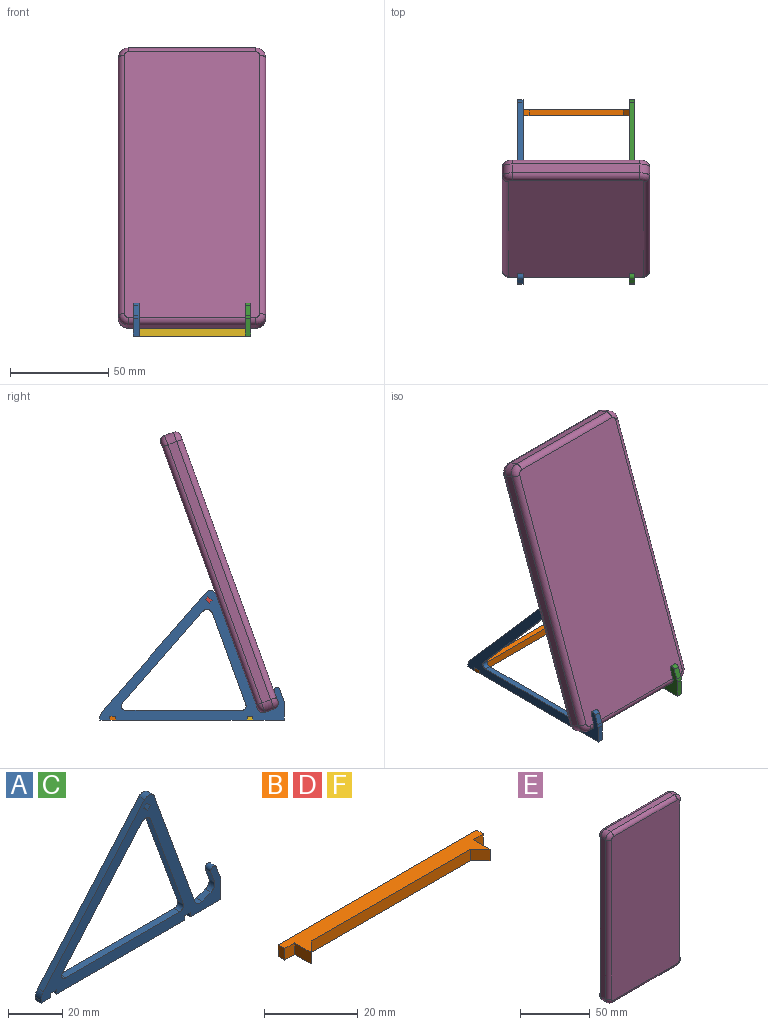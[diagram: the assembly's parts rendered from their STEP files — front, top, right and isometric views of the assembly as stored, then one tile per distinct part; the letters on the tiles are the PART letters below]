
ASSEMBLY  parts=6 mates=15
PART A: 34 faces, bbox 93.9x3x66 mm
  f0: plane 67x3mm, normal (0,0,-1), area 201mm2, adj f2,f3,f24,f28
  f1: plane 15.88x3mm, normal (0,0,-1), area 47.6mm2, adj f2,f3,f14,f25
  f2: plane 93.88x65.98mm, normal (0,-1,0), area 1195.2mm2, adj f0,f1,f4,f5,f6,f7,f8,f9
  f3: plane 93.88x65.98mm, normal (0,1,0), area 1195.2mm2, adj f0,f1,f4,f5,f6,f7,f8,f9
  f4: plane 5x3mm, normal (0,0,-1), area 15mm2, adj f2,f3,f13,f27
  f5: plane 5.33x3mm, normal (0.94,0,0.34), area 17mm2, adj f2,f3,f16,f17
  f6: plane 58.19x21.18mm, normal (0.94,0,0.34), area 185.8mm2, adj f2,f3,f10,f12
  f7: plane 60.54x52.87mm, normal (-0.75,0,0.66), area 241.1mm2, adj f2,f3,f10,f15
  f8: plane 5.17x3mm, normal (-0.94,0,-0.34), area 16.5mm2, adj f2,f3,f11,f17
  f9: plane 4.7x3mm, normal (-0.34,0,0.94), area 15mm2, adj f2,f3,f11,f12
  f10: cylinder r=3mm len=5.08mm, axis (0,1,0), area 18.7mm2, adj f2,f3,f6,f7
  f11: cylinder r=3mm len=3.85mm, axis (0,1,0), area 14.1mm2, adj f2,f3,f8,f9
  f12: cylinder r=3mm len=3.85mm, axis (0,1,0), area 14.1mm2, adj f2,f3,f6,f9
  f13: plane 3x1.12mm, normal (-1,0,0), area 3.4mm2, adj f2,f3,f4,f15
  f14: plane 8.73x3mm, normal (1,0,0), area 26.2mm2, adj f1,f2,f3,f16
  f15: cylinder r=5mm len=3.29mm, axis (0,-1,0), area 10.8mm2, adj f2,f3,f7,f13
  f16: cylinder r=5mm len=3mm, axis (0,-1,0), area 5.2mm2, adj f2,f3,f5,f14
  f17: cylinder r=1.5mm len=3mm, axis (0,1,0), area 14.1mm2, adj f2,f3,f5,f8
  f18: cylinder r=2mm len=3mm, axis (0,-1,0), area 11.5mm2, adj f2,f3,f19,f23
  f19: plane 46.66x16.98mm, normal (-0.94,0,-0.34), area 149mm2, adj f2,f3,f18,f20
  f20: cylinder r=3mm len=5.08mm, axis (0,-1,0), area 18.7mm2, adj f2,f3,f19,f21
  f21: plane 46.97x41.02mm, normal (0.75,0,-0.66), area 187.1mm2, adj f2,f3,f20,f22
  f22: cylinder r=2mm len=3.32mm, axis (0,-1,0), area 13.7mm2, adj f2,f3,f21,f23
  f23: plane 59.7x3mm, normal (0,0,1), area 179.1mm2, adj f2,f3,f18,f22
  f24: plane 3x2mm, normal (1,0,0), area 6mm2, adj f0,f2,f3,f26
  f25: plane 3x2mm, normal (-1,0,0), area 6mm2, adj f1,f2,f3,f26
  f26: plane 3x3mm, normal (0,0,-1), area 9mm2, adj f2,f3,f24,f25
  f27: plane 3x2mm, normal (1,0,0), area 6mm2, adj f2,f3,f4,f29
  f28: plane 3x2mm, normal (-1,0,0), area 6mm2, adj f0,f2,f3,f29
  f29: plane 3x3mm, normal (0,0,-1), area 9mm2, adj f2,f3,f27,f28
  f30: plane 3x1.51mm, normal (-0.75,0,0.66), area 6mm2, adj f2,f3,f31,f33
  f31: plane 3x2.26mm, normal (-0.66,0,-0.75), area 9mm2, adj f2,f3,f30,f32
  f32: plane 3x1.51mm, normal (0.75,0,-0.66), area 6mm2, adj f2,f3,f31,f33
  f33: plane 3x2.26mm, normal (0.66,0,0.75), area 9mm2, adj f2,f3,f30,f32
PART B: 12 faces, bbox 60x7x3 mm
  f0: plane 3x3mm, normal (0,-1,0), area 9mm2, adj f1,f2,f4,f9
  f1: plane 3x2mm, normal (1,0,0), area 6mm2, adj f0,f2,f4,f6
  f2: plane 60x7mm, normal (0,0,1), area 237mm2, adj f0,f1,f3,f5,f6,f7,f8,f9
  f3: plane 3x2mm, normal (-1,0,0), area 6mm2, adj f2,f4,f5,f6
  f4: plane 60x7mm, normal (0,0,-1), area 237mm2, adj f0,f1,f3,f5,f6,f7,f8,f9
  f5: plane 3x3mm, normal (0,-1,0), area 9mm2, adj f2,f3,f4,f7
  f6: plane 60x3mm, normal (0,1,0), area 180mm2, adj f1,f2,f3,f4
  f7: plane 5x3mm, normal (-1,0,0), area 15mm2, adj f2,f4,f5,f8
  f8: plane 3x3mm, normal (0.71,-0.71,0), area 12.7mm2, adj f2,f4,f7,f11
  f9: plane 5x3mm, normal (1,0,0), area 15mm2, adj f0,f2,f4,f10
  f10: plane 3x3mm, normal (-0.71,-0.71,0), area 12.7mm2, adj f2,f4,f9,f11
  f11: plane 48x3mm, normal (0,-1,0), area 144mm2, adj f2,f4,f8,f10
PART C: same geometry as A
PART D: same geometry as B
PART E: 26 faces, bbox 75x10.8x150 mm
  f0: plane 140x4.8mm, normal (1,0,0), area 672mm2, adj f1,f7,f13,f21
  f1: cylinder r=5mm len=5mm, axis (0,1,0), area 37.7mm2, adj f0,f2,f15,f23
  f2: plane 65x4.8mm, normal (0,0,1), area 312mm2, adj f1,f3,f17,f25
  f3: cylinder r=5mm len=5mm, axis (0,1,0), area 37.7mm2, adj f2,f4,f16,f24
  f4: plane 140x4.8mm, normal (-1,0,0), area 672mm2, adj f3,f5,f14,f22
  f5: cylinder r=5mm len=5mm, axis (0,1,0), area 37.7mm2, adj f4,f6,f12,f20
  f6: plane 65x4.8mm, normal (0,0,-1), area 312mm2, adj f5,f7,f10,f18
  f7: cylinder r=5mm len=5mm, axis (0,1,0), area 37.7mm2, adj f0,f6,f11,f19
  f8: plane 144x69mm, normal (0,-1,0), area 9932.6mm2, adj f18,f19,f20,f21,f22,f23,f24,f25
  f9: plane 144x69mm, normal (0,1,0), area 9932.6mm2, adj f10,f11,f12,f13,f14,f15,f16,f17
  f10: cylinder r=3mm len=65mm, axis (1,0,0), area 306.3mm2, adj f6,f9,f11,f12
  f11: torus R=2mm, axis (0,-1,0), area 28.9mm2, adj f7,f9,f10,f13
  f12: torus R=2mm, axis (0,-1,0), area 28.9mm2, adj f5,f9,f10,f14
  f13: cylinder r=3mm len=140mm, axis (0,0,1), area 659.7mm2, adj f0,f9,f11,f15
  f14: cylinder r=3mm len=140mm, axis (0,0,-1), area 659.7mm2, adj f4,f9,f12,f16
  f15: torus R=2mm, axis (0,-1,0), area 28.9mm2, adj f1,f9,f13,f17
  f16: torus R=2mm, axis (0,-1,0), area 28.9mm2, adj f3,f9,f14,f17
  f17: cylinder r=3mm len=65mm, axis (-1,0,0), area 306.3mm2, adj f2,f9,f15,f16
  f18: cylinder r=3mm len=65mm, axis (-1,0,0), area 306.3mm2, adj f6,f8,f19,f20
  f19: torus R=2mm, axis (0,-1,0), area 28.9mm2, adj f7,f8,f18,f21
  f20: torus R=2mm, axis (0,-1,0), area 28.9mm2, adj f5,f8,f18,f22
  f21: cylinder r=3mm len=140mm, axis (0,0,-1), area 659.7mm2, adj f0,f8,f19,f23
  f22: cylinder r=3mm len=140mm, axis (0,0,1), area 659.7mm2, adj f4,f8,f20,f24
  f23: torus R=2mm, axis (0,-1,0), area 28.9mm2, adj f1,f8,f21,f25
  f24: torus R=2mm, axis (0,-1,0), area 28.9mm2, adj f3,f8,f22,f25
  f25: cylinder r=3mm len=65mm, axis (1,0,0), area 306.3mm2, adj f2,f8,f23,f24
PART F: same geometry as B
PLACE A rot(axis=(0,0,-1),90deg) t=(-33.49,32.48,-36.6)mm
PLACE B rot(axis=(0,-0.71,0.71),180deg) t=(-4.99,23.36,-36.6)mm
PLACE C rot(axis=(0,0,-1),90deg) t=(23.51,32.48,-36.6)mm fixed
PLACE D rot(axis=(0,0.41,0.91),180deg) t=(-4.99,-26.22,25.29)mm
PLACE E rot(axis=(-1,0,0),20deg) t=(-5.04,-25.88,36.87)mm
PLACE F rot(axis=(0,0.71,-0.71),180deg) t=(-4.99,-46.64,-36.6)mm
MATE planar C.f25 <-> F.f2  axis (0,1,0) through (23.51,-48.14,-35.6)mm
MATE planar B.f1 <-> A.f2  axis (-1,0,0) through (-34.99,23.36,-35.6)mm
MATE parallel C.f2 <-> A.f2  axis (-1,0,0) through (22.01,-1.93,-4.8)mm
MATE planar D.f1 <-> A.f2  axis (-1,0,0) through (-34.99,-25.56,24.54)mm
MATE planar C.f0 <-> A.f0  axis (0,0,-1) through (23.51,-11.64,-36.6)mm
MATE planar F.f5 <-> C.f26  axis (0,0,1) through (23.51,-46.64,-34.6)mm
MATE planar A.f30 <-> D.f4  axis (0,0.75,0.66) through (-33.49,-26.69,23.55)mm
MATE planar B.f0 <-> C.f29  axis (0,0,1) through (-33.49,23.36,-34.6)mm
MATE planar C.f9 <-> E.f6  axis (0,0.34,0.94) through (23.51,-56.7,-31.72)mm
MATE planar C.f13 <-> A.f13  axis (0,1,0) through (23.51,29.86,-36.04)mm
MATE planar B.f2 <-> A.f28  axis (0,-1,0) through (-4.99,21.86,-34.54)mm
MATE planar D.f0 <-> A.f33  axis (0,0.66,-0.75) through (-33.49,-24.91,23.79)mm
MATE planar F.f3 <-> C.f3  axis (1,0,0) through (25.01,-46.64,-35.6)mm
MATE planar F.f1 <-> A.f2  axis (-1,0,0) through (-34.99,-46.64,-35.6)mm
MATE planar E.f9 <-> C.f6  axis (0,0.94,-0.34) through (-5.04,-25.88,36.87)mm
